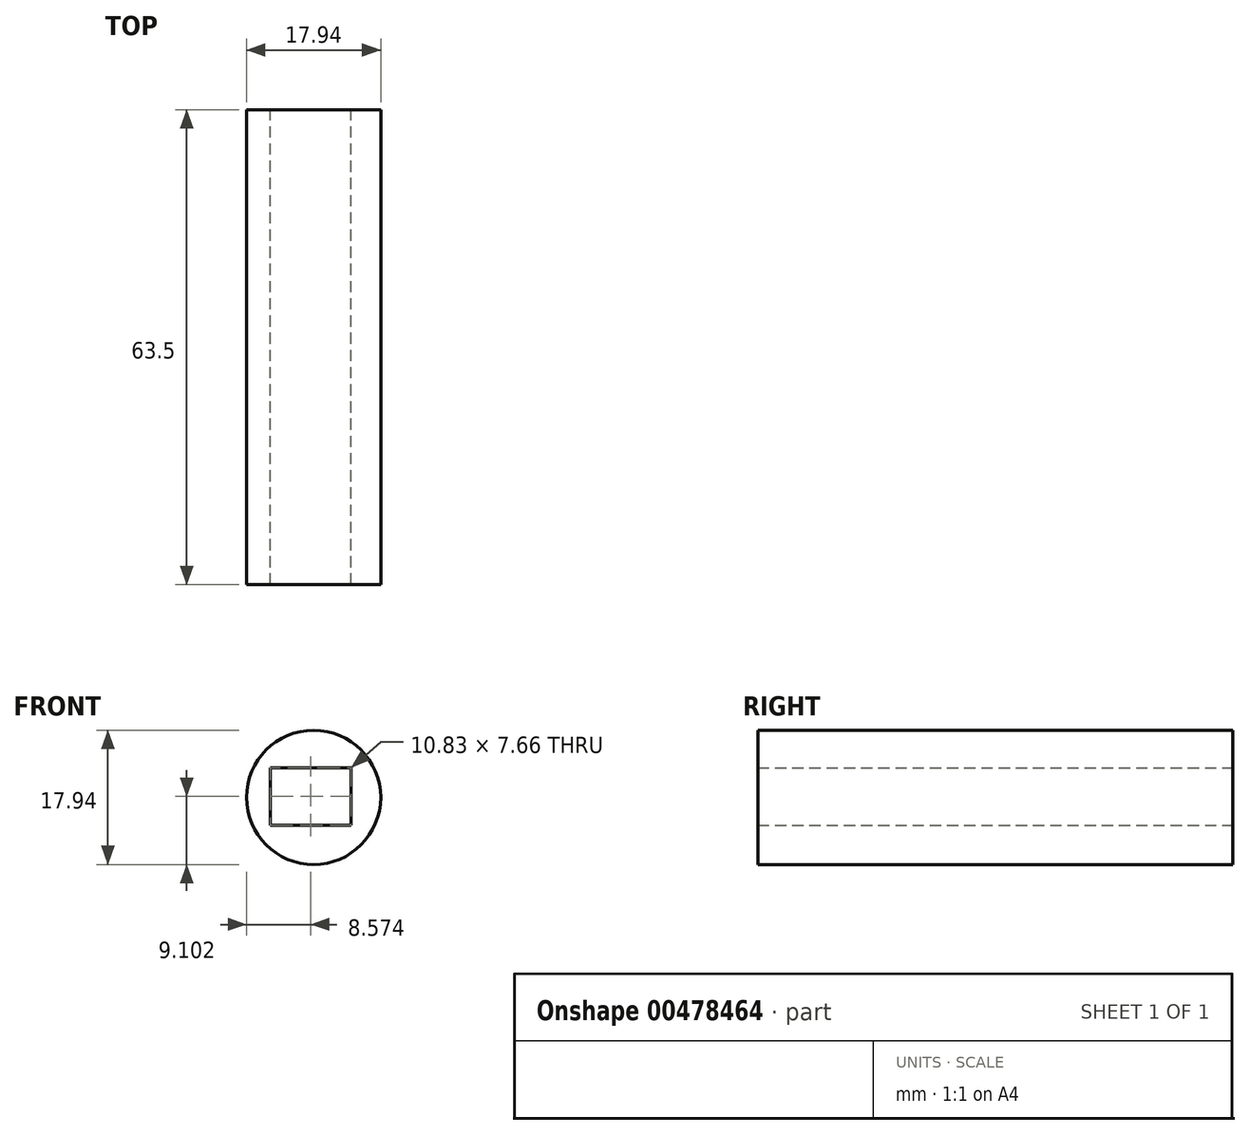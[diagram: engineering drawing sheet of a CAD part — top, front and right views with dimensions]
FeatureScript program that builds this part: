
annotation { "Feature Type Name" : "Feature", "Feature Type Description" : "" }
export const myFeature = defineFeature(function(context is Context, id is Id, definition is map)
    precondition{}
    {
        {
            var Q0;
            Q0=qCreatedBy(makeId("Front.planeOp"),FACE);
            var sketch = newSketch(context, id + "F0", { "sketchPlane" : qUnion([Q0])});
            skCircle(sketch, "E0", {"center": v(0, 0) * mm, "radius": 8.97 * mm});
            skLineSegment(sketch, "E1.bottom", {"start": v(-5.8, 3.96) * mm, "end": v(5.02, 3.96) * mm});
            skLineSegment(sketch, "E1.top", {"start": v(-5.8, -3.7) * mm, "end": v(5.02, -3.7) * mm});
            skLineSegment(sketch, "E1.left", {"start": v(-5.8, 3.96) * mm, "end": v(-5.8, -3.7) * mm});
            skLineSegment(sketch, "E1.right", {"start": v(5.02, 3.96) * mm, "end": v(5.02, -3.7) * mm});
            skSolve(sketch);
        }
        {
            var Q0;
            Q0=makeQuery(id+"F0.imprint","IMPRINT",FACE,{"disambiguationData":[TD([[makeQuery(id+"F0.imprint","IMPRINT",EDGE,{"derivedFrom":sQuery(id+"F0.wireOp",EDGE,"E0")}),1.0]])]});
            extrude(context, id + "F1", {"entities" : qUnion([Q0]), "depth" : 50.8 * mm});
        }
        {
            var Q0;
            Q0=makeQuery(id+"F1.opExtrude","CAP_FACE",FACE,{"disambiguationData":[OSD([sQuery(id+"F0.wireOp",EDGE,"E0"),sQuery(id+"F0.wireOp",EDGE,"E1.bottom"),sQuery(id+"F0.wireOp",EDGE,"E1.top"),sQuery(id+"F0.wireOp",EDGE,"E1.left"),sQuery(id+"F0.wireOp",EDGE,"E1.right")])],"isStart":false});
            extrude(context, id + "F2", {"entities" : qUnion([Q0]), "operationType" : NewBodyOperationType.ADD, "endBound" : BoundingType.SYMMETRIC, "depth" : 25.4 * mm});
        }
    });
